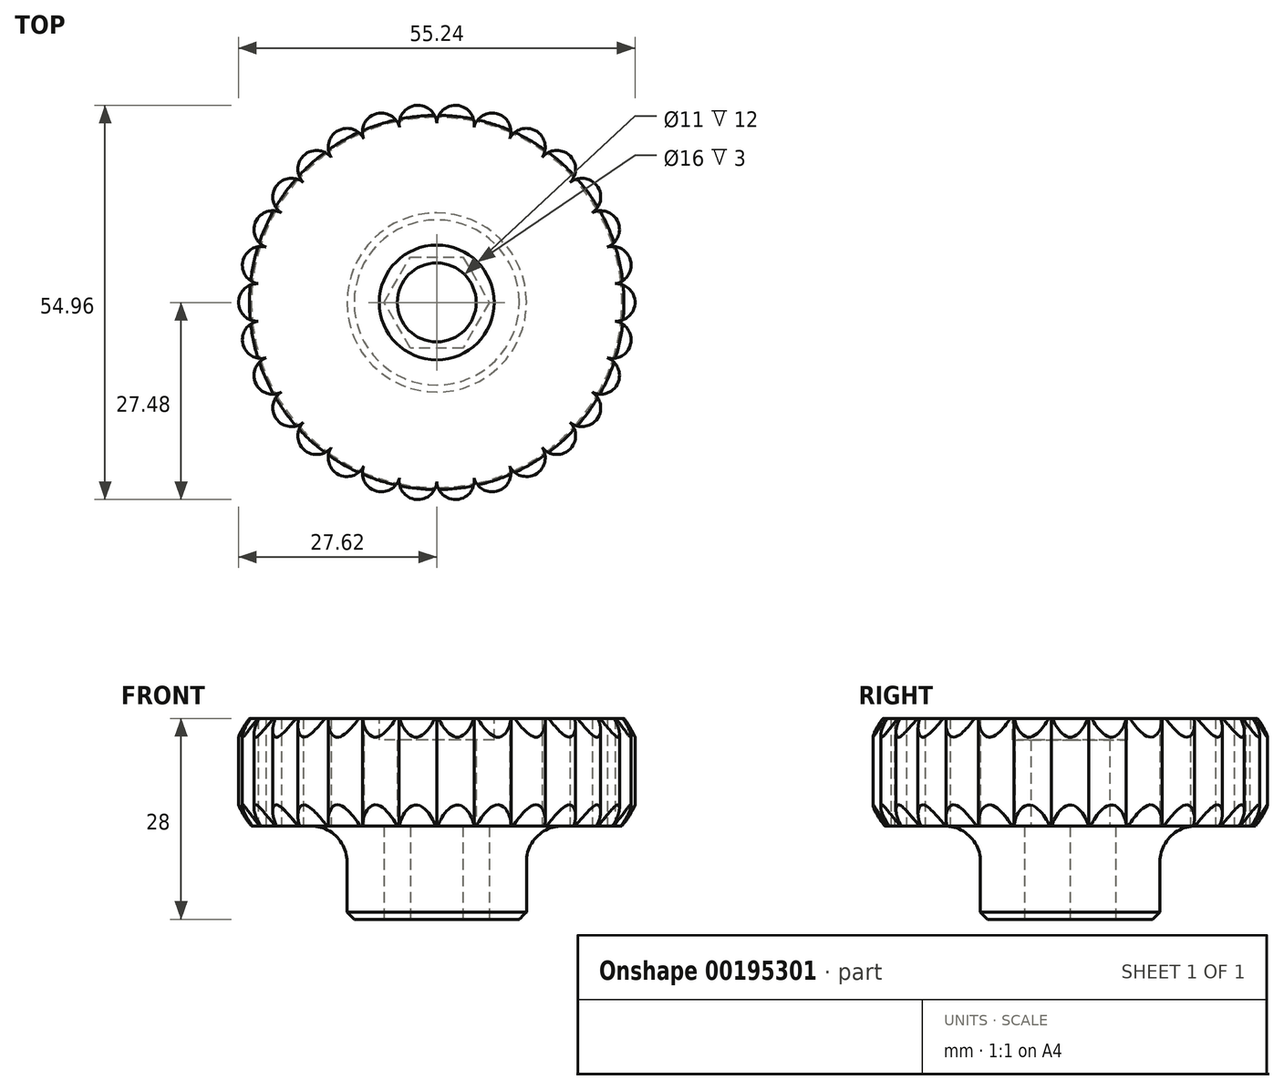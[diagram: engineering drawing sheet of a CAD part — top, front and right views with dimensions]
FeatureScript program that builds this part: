
annotation { "Feature Type Name" : "Feature", "Feature Type Description" : "" }
export const myFeature = defineFeature(function(context is Context, id is Id, definition is map)
    precondition{}
    {
        {
            var Q0;
            Q0=qCreatedBy(makeId("Top.planeOp"),FACE);
            var sketch = newSketch(context, id + "F0", { "sketchPlane" : qUnion([Q0])});
            skCircle(sketch, "E0", {"center": v(0, 0) * mm, "radius": 12.5 * mm});
            skCircle(sketch, "E1.cCircle", {"center": v(0, 0) * mm, "radius": 6.35 * mm, "construction": true});
            skLineSegment(sketch, "E1.0", {"start": v(7.33, 0) * mm, "end": v(3.67, -6.35) * mm});
            skLineSegment(sketch, "E1.1", {"start": v(3.67, -6.35) * mm, "end": v(-3.67, -6.35) * mm});
            skLineSegment(sketch, "E1.2", {"start": v(-3.67, -6.35) * mm, "end": v(-7.33, 0) * mm});
            skLineSegment(sketch, "E1.3", {"start": v(-7.33, 0) * mm, "end": v(-3.67, 6.35) * mm});
            skLineSegment(sketch, "E1.4", {"start": v(-3.67, 6.35) * mm, "end": v(3.67, 6.35) * mm});
            skLineSegment(sketch, "E1.5", {"start": v(3.67, 6.35) * mm, "end": v(7.33, 0) * mm});
            skPoint(sketch, "E1.0.midPoint", {"position": v(5.5, -3.17) * mm});
            skSolve(sketch);
        }
        {
            var Q0;
            Q0 = qSketchRegion(id + "F0", true);
            extrude(context, id + "F1", {"entities" : qUnion([Q0]), "depth" : 13 * mm});
        }
        {
            var Q0;
            Q0=makeQuery(id+"F1.opExtrude","CAP_FACE",FACE,{"disambiguationData":[OSD([sQuery(id+"F0.wireOp",EDGE,"E0"),sQuery(id+"F0.wireOp",EDGE,"E1.0"),sQuery(id+"F0.wireOp",EDGE,"E1.1"),sQuery(id+"F0.wireOp",EDGE,"E1.2"),sQuery(id+"F0.wireOp",EDGE,"E1.3"),sQuery(id+"F0.wireOp",EDGE,"E1.4"),sQuery(id+"F0.wireOp",EDGE,"E1.5")])],"isStart":false});
            var sketch = newSketch(context, id + "F2", { "sketchPlane" : qUnion([Q0])});
            skCircle(sketch, "E2", {"center": v(0, 0) * mm, "radius": 25 * mm});
            skCircle(sketch, "E3", {"center": v(0, 0) * mm, "radius": 5.5 * mm});
            skArc(sketch, "E4", {"start": v(5.2, 24.45) * mm, "mid": v(2.89, 27.47) * mm, "end": v(0, 25) * mm});
            skArc(sketch, "E5.1.0", {"start": v(10.17, 22.84) * mm, "mid": v(8.53, 26.27) * mm, "end": v(5.2, 24.45) * mm});
            skArc(sketch, "E5.2.0", {"start": v(14.7, 20.23) * mm, "mid": v(13.8, 23.92) * mm, "end": v(10.17, 22.84) * mm});
            skArc(sketch, "E5.3.0", {"start": v(18.58, 16.73) * mm, "mid": v(18.48, 20.52) * mm, "end": v(14.7, 20.23) * mm});
            skArc(sketch, "E5.4.0", {"start": v(21.65, 12.5) * mm, "mid": v(22.34, 16.23) * mm, "end": v(18.58, 16.73) * mm});
            skArc(sketch, "E5.5.0", {"start": v(23.78, 7.73) * mm, "mid": v(25.23, 11.23) * mm, "end": v(21.65, 12.5) * mm});
            skArc(sketch, "E5.6.0", {"start": v(24.86, 2.61) * mm, "mid": v(27.01, 5.74) * mm, "end": v(23.78, 7.73) * mm});
            skArc(sketch, "E5.7.0", {"start": v(24.86, -2.61) * mm, "mid": v(27.62, 0) * mm, "end": v(24.86, 2.61) * mm});
            skArc(sketch, "E5.8.0", {"start": v(23.78, -7.73) * mm, "mid": v(27.01, -5.74) * mm, "end": v(24.86, -2.61) * mm});
            skArc(sketch, "E5.9.0", {"start": v(21.65, -12.5) * mm, "mid": v(25.23, -11.23) * mm, "end": v(23.78, -7.73) * mm});
            skArc(sketch, "E5.10.0", {"start": v(18.58, -16.73) * mm, "mid": v(22.34, -16.23) * mm, "end": v(21.65, -12.5) * mm});
            skArc(sketch, "E5.11.0", {"start": v(14.7, -20.23) * mm, "mid": v(18.48, -20.52) * mm, "end": v(18.58, -16.73) * mm});
            skArc(sketch, "E5.12.0", {"start": v(10.17, -22.84) * mm, "mid": v(13.8, -23.92) * mm, "end": v(14.7, -20.23) * mm});
            skArc(sketch, "E5.13.0", {"start": v(5.2, -24.45) * mm, "mid": v(8.53, -26.27) * mm, "end": v(10.17, -22.84) * mm});
            skArc(sketch, "E5.14.0", {"start": v(0, -25) * mm, "mid": v(2.89, -27.47) * mm, "end": v(5.2, -24.45) * mm});
            skArc(sketch, "E5.15.0", {"start": v(-5.2, -24.45) * mm, "mid": v(-2.89, -27.47) * mm, "end": v(0, -25) * mm});
            skArc(sketch, "E5.16.0", {"start": v(-10.17, -22.84) * mm, "mid": v(-8.53, -26.27) * mm, "end": v(-5.2, -24.45) * mm});
            skArc(sketch, "E5.17.0", {"start": v(-14.7, -20.23) * mm, "mid": v(-13.8, -23.92) * mm, "end": v(-10.17, -22.84) * mm});
            skArc(sketch, "E5.18.0", {"start": v(-18.58, -16.73) * mm, "mid": v(-18.48, -20.52) * mm, "end": v(-14.7, -20.23) * mm});
            skArc(sketch, "E5.19.0", {"start": v(-21.65, -12.5) * mm, "mid": v(-22.34, -16.23) * mm, "end": v(-18.58, -16.73) * mm});
            skArc(sketch, "E5.20.0", {"start": v(-23.78, -7.73) * mm, "mid": v(-25.23, -11.23) * mm, "end": v(-21.65, -12.5) * mm});
            skArc(sketch, "E5.21.0", {"start": v(-24.86, -2.61) * mm, "mid": v(-27.01, -5.74) * mm, "end": v(-23.78, -7.73) * mm});
            skArc(sketch, "E5.22.0", {"start": v(-24.86, 2.61) * mm, "mid": v(-27.62, 0) * mm, "end": v(-24.86, -2.61) * mm});
            skArc(sketch, "E5.23.0", {"start": v(-23.78, 7.73) * mm, "mid": v(-27.01, 5.74) * mm, "end": v(-24.86, 2.61) * mm});
            skArc(sketch, "E5.24.0", {"start": v(-21.65, 12.5) * mm, "mid": v(-25.23, 11.23) * mm, "end": v(-23.78, 7.73) * mm});
            skArc(sketch, "E5.25.0", {"start": v(-18.58, 16.73) * mm, "mid": v(-22.34, 16.23) * mm, "end": v(-21.65, 12.5) * mm});
            skArc(sketch, "E5.26.0", {"start": v(-14.7, 20.23) * mm, "mid": v(-18.48, 20.52) * mm, "end": v(-18.58, 16.73) * mm});
            skArc(sketch, "E5.27.0", {"start": v(-10.17, 22.84) * mm, "mid": v(-13.8, 23.92) * mm, "end": v(-14.7, 20.23) * mm});
            skArc(sketch, "E5.28.0", {"start": v(-5.2, 24.45) * mm, "mid": v(-8.53, 26.27) * mm, "end": v(-10.17, 22.84) * mm});
            skArc(sketch, "E5.29.0", {"start": v(0, 25) * mm, "mid": v(-2.89, 27.47) * mm, "end": v(-5.2, 24.45) * mm});
            skLineSegment(sketch, "E5.anchor1", {"start": v(0, 0) * mm, "end": v(0, 25) * mm, "construction": true});
            skLineSegment(sketch, "E5.anchor2", {"start": v(0, 0) * mm, "end": v(-5.2, 24.45) * mm, "construction": true});
            skSolve(sketch);
        }
        {
            var Q0;
            Q0 = qSketchRegion(id + "F2", true);
            extrude(context, id + "F3", {"entities" : qUnion([Q0]), "operationType" : NewBodyOperationType.ADD, "depth" : 15 * mm});
        }
        {
            var Q0;
            Q0=makeQuery(id+"F3.opExtrude","CAP_FACE",FACE,{"disambiguationData":[OSD([sQuery(id+"F2.wireOp",EDGE,"E3"),sQuery(id+"F2.wireOp",EDGE,"E4"),sQuery(id+"F2.wireOp",EDGE,"E5.1.0"),sQuery(id+"F2.wireOp",EDGE,"E5.2.0"),sQuery(id+"F2.wireOp",EDGE,"E5.3.0"),sQuery(id+"F2.wireOp",EDGE,"E5.4.0"),sQuery(id+"F2.wireOp",EDGE,"E5.5.0"),sQuery(id+"F2.wireOp",EDGE,"E5.6.0"),sQuery(id+"F2.wireOp",EDGE,"E5.7.0"),sQuery(id+"F2.wireOp",EDGE,"E5.8.0"),sQuery(id+"F2.wireOp",EDGE,"E5.9.0"),sQuery(id+"F2.wireOp",EDGE,"E5.10.0"),sQuery(id+"F2.wireOp",EDGE,"E5.11.0"),sQuery(id+"F2.wireOp",EDGE,"E5.12.0"),sQuery(id+"F2.wireOp",EDGE,"E5.13.0"),sQuery(id+"F2.wireOp",EDGE,"E5.14.0"),sQuery(id+"F2.wireOp",EDGE,"E5.15.0"),sQuery(id+"F2.wireOp",EDGE,"E5.16.0"),sQuery(id+"F2.wireOp",EDGE,"E5.17.0"),sQuery(id+"F2.wireOp",EDGE,"E5.18.0"),sQuery(id+"F2.wireOp",EDGE,"E5.19.0"),sQuery(id+"F2.wireOp",EDGE,"E5.20.0"),sQuery(id+"F2.wireOp",EDGE,"E5.21.0"),sQuery(id+"F2.wireOp",EDGE,"E5.22.0"),sQuery(id+"F2.wireOp",EDGE,"E5.23.0"),sQuery(id+"F2.wireOp",EDGE,"E5.24.0"),sQuery(id+"F2.wireOp",EDGE,"E5.25.0"),sQuery(id+"F2.wireOp",EDGE,"E5.26.0"),sQuery(id+"F2.wireOp",EDGE,"E5.27.0"),sQuery(id+"F2.wireOp",EDGE,"E5.28.0"),sQuery(id+"F2.wireOp",EDGE,"E5.29.0")])],"isStart":false});
            var sketch = newSketch(context, id + "F4", { "sketchPlane" : qUnion([Q0])});
            skCircle(sketch, "E6", {"center": v(0, 0) * mm, "radius": 8 * mm});
            skSolve(sketch);
        }
        {
            var Q0;
            Q0 = qSketchRegion(id + "F4", true);
            extrude(context, id + "F5", {"entities" : qUnion([Q0]), "operationType" : NewBodyOperationType.REMOVE, "oppositeDirection" : true, "depth" : 3 * mm});
        }
        {
            var Q0;
            Q0=makeQuery(id+"F1.opExtrude","CAP_EDGE",EDGE,{"disambiguationData":[OSD([sQuery(id+"F0.wireOp",EDGE,"E0")])],"isStart":false});
            fillet(context, id + "F6", {"entities" : qUnion([Q0]), "radius" : 5 * mm, "tangentPropagation" : true, "allowEdgeOverflow" : false});
        }
        {
            var Q0;
            Q0=makeQuery(id+"F1.opExtrude","CAP_EDGE",EDGE,{"disambiguationData":[OSD([sQuery(id+"F0.wireOp",EDGE,"E0")])],"isStart":true});
            chamfer(context, id + "F7", {"entities" : qUnion([Q0]), "width" : 1 * mm, "tangentPropagation" : true});
        }
        {
            var Q0;
            Q0=qCreatedBy(makeId("Front.planeOp"),FACE);
            var sketch = newSketch(context, id + "F8", { "sketchPlane" : qUnion([Q0])});
            skArc(sketch, "E7", {"start": v(23.56, 10.93) * mm, "mid": v(28.59, 20.67) * mm, "end": v(23.56, 30.41) * mm});
            skLineSegment(sketch, "E8", {"start": v(23.56, 10.93) * mm, "end": v(54.84, 10.93) * mm});
            skLineSegment(sketch, "E9", {"start": v(54.84, 10.93) * mm, "end": v(54.84, 30.41) * mm});
            skLineSegment(sketch, "E10", {"start": v(54.84, 30.41) * mm, "end": v(23.56, 30.41) * mm});
            skSolve(sketch);
        }
        {
            var Q0;
            Q0 = qSketchRegion(id + "F8", true);
            var Q1;
            Q1=makeQuery(id+"F5.boolean.opBoolean","INTERSECT",EDGE,{"derivedFrom":[makeQuery(id+"F3.opExtrude","SWEPT_FACE",FACE,{"disambiguationData":[OSD([sQuery(id+"F2.wireOp",EDGE,"E3")])]}),makeQuery(id+"F5.opExtrude","CAP_FACE",FACE,{"disambiguationData":[OSD([sQuery(id+"F4.wireOp",EDGE,"E6")])],"isStart":false})]});
            revolve(context, id + "F9", {"entities" : qUnion([Q0]), "axis" : qUnion([Q1]), "revolveType" : RevolveType.FULL});
        }
        {
            var Q0;
            Q0=makeQuery(id+"F9.opRevolve","SWEPT_BODY",BODY,{"disambiguationData":[OSD([sQuery(id+"F8.wireOp",EDGE,"E7"),sQuery(id+"F8.wireOp",EDGE,"E8"),sQuery(id+"F8.wireOp",EDGE,"E9"),sQuery(id+"F8.wireOp",EDGE,"E10")])]});
            var Q1;
            Q1=makeQuery(id+"F1.opExtrude","SWEPT_BODY",BODY,{"disambiguationData":[OSD([sQuery(id+"F0.wireOp",EDGE,"E0"),sQuery(id+"F0.wireOp",EDGE,"E1.0"),sQuery(id+"F0.wireOp",EDGE,"E1.1"),sQuery(id+"F0.wireOp",EDGE,"E1.2"),sQuery(id+"F0.wireOp",EDGE,"E1.3"),sQuery(id+"F0.wireOp",EDGE,"E1.4"),sQuery(id+"F0.wireOp",EDGE,"E1.5")])]});
            booleanBodies(context, id + "F10", {"operationType" : BooleanOperationType.SUBTRACTION, "tools" : qUnion([Q0]), "targets" : qUnion([Q1])});
        }
    });
